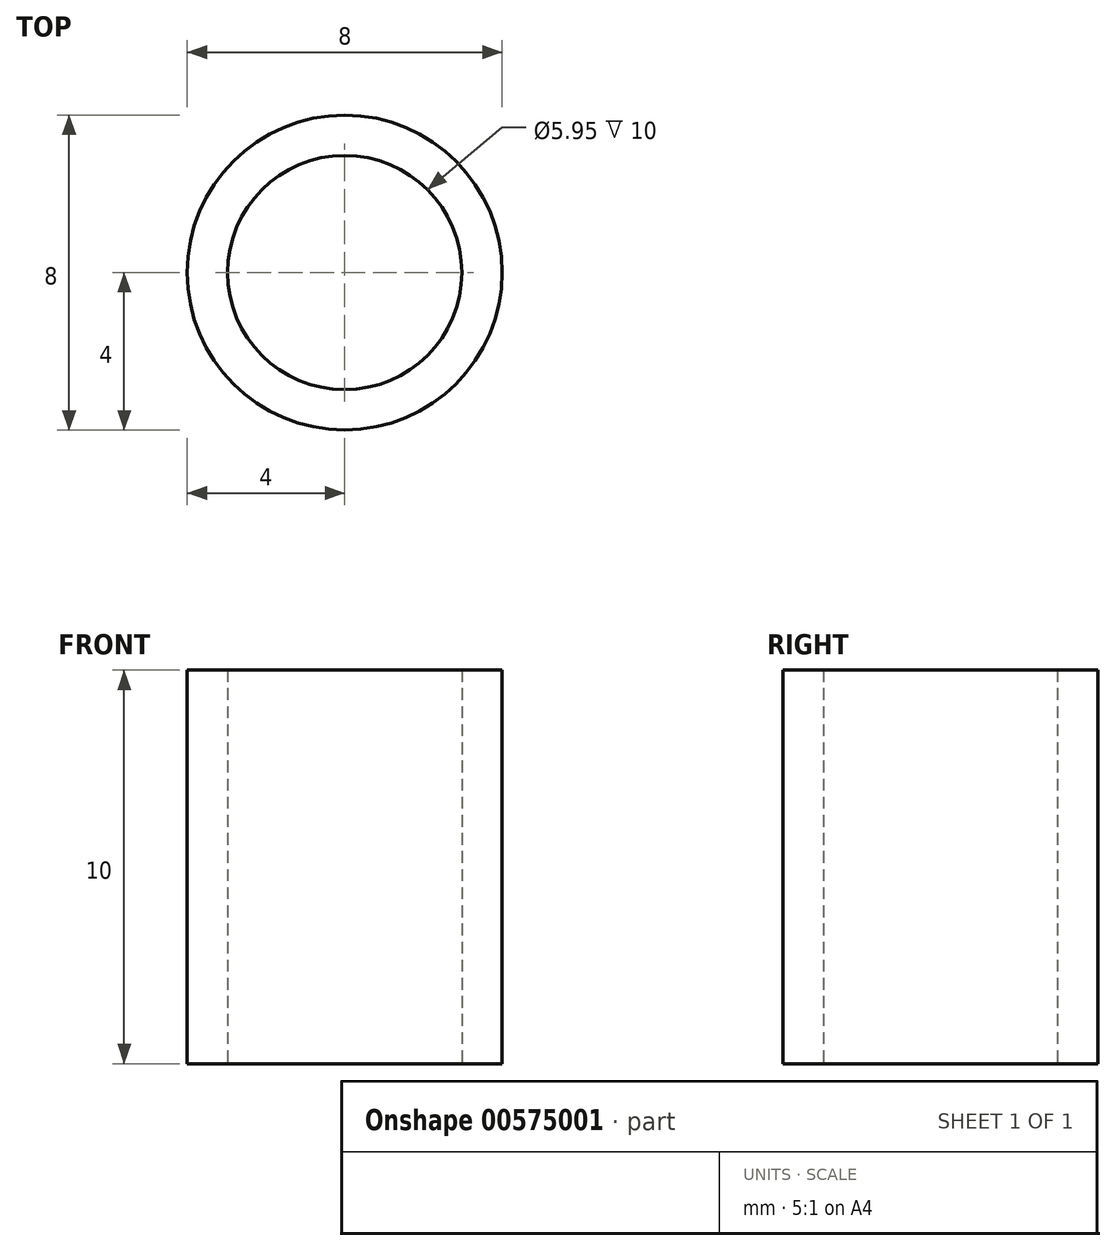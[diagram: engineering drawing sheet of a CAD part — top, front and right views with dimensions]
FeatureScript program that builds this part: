
annotation { "Feature Type Name" : "Feature", "Feature Type Description" : "" }
export const myFeature = defineFeature(function(context is Context, id is Id, definition is map)
    precondition{}
    {
        {
            var Q0;
            Q0=qCreatedBy(makeId("Top.planeOp"),FACE);
            var sketch = newSketch(context, id + "F0", { "sketchPlane" : qUnion([Q0])});
            skCircle(sketch, "E0", {"center": v(0, 0) * mm, "radius": 4 * mm});
            skCircle(sketch, "E1", {"center": v(0, 0) * mm, "radius": 2.98 * mm});
            skPoint(sketch, "E2", {"position": v(2.98, 0) * mm});
            skPoint(sketch, "E3", {"position": v(4, 0) * mm});
            skSolve(sketch);
        }
        {
            var Q0;
            Q0 = qSketchRegion(id + "F0", true);
            extrude(context, id + "F1", {"entities" : qUnion([Q0]), "depth" : 10 * mm, "offsetDistance" : 25 * mm});
        }
    });
